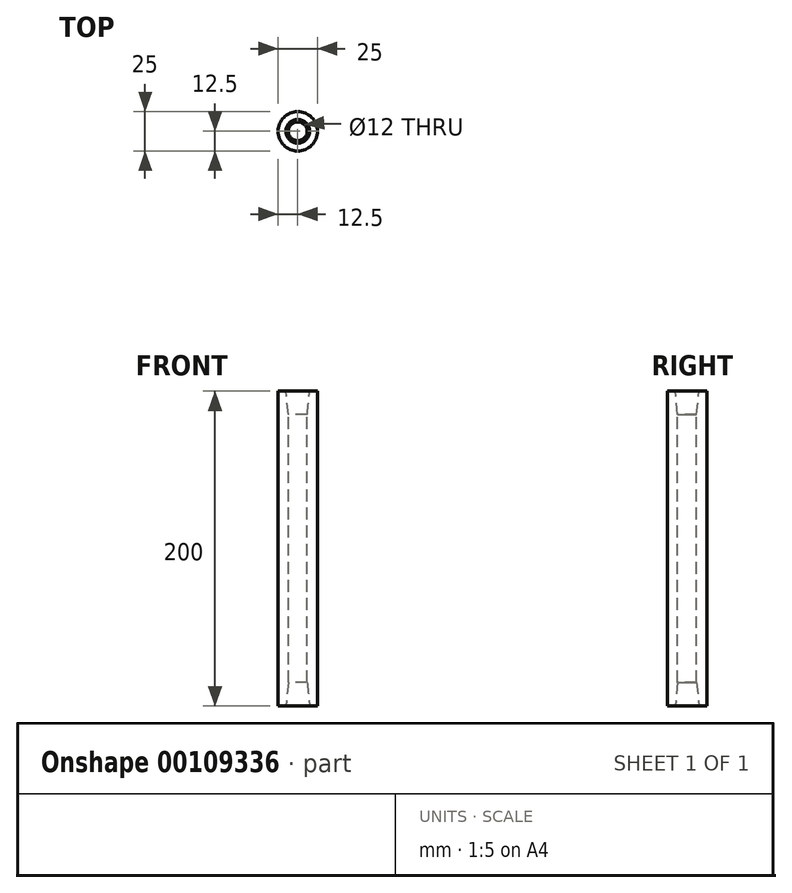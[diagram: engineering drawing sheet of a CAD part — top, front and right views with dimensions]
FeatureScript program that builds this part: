
annotation { "Feature Type Name" : "Feature", "Feature Type Description" : "" }
export const myFeature = defineFeature(function(context is Context, id is Id, definition is map)
    precondition{}
    {
        {
            var Q0;
            Q0=qCreatedBy(makeId("Front.planeOp"),FACE);
            var sketch = newSketch(context, id + "F0", { "sketchPlane" : qUnion([Q0])});
            skLineSegment(sketch, "E0.bottom", {"start": v(-6, 50) * mm, "end": v(0, 50) * mm});
            skLineSegment(sketch, "E0.top", {"start": v(-6, -120) * mm, "end": v(0, -120) * mm});
            skLineSegment(sketch, "E0.left", {"start": v(-6, 50) * mm, "end": v(-6, -120) * mm});
            skLineSegment(sketch, "E1", {"start": v(-6, 50) * mm, "end": v(-7.5, 65) * mm});
            skLineSegment(sketch, "E2", {"start": v(-7.5, 65) * mm, "end": v(0, 65) * mm});
            skLineSegment(sketch, "E3", {"start": v(-6, -120) * mm, "end": v(-7.5, -135) * mm});
            skLineSegment(sketch, "E4", {"start": v(-7.5, -135) * mm, "end": v(0, -135) * mm});
            skPoint(sketch, "E5", {"position": v(0, 50) * mm});
            skPoint(sketch, "E6", {"position": v(0, 65) * mm});
            skPoint(sketch, "E7", {"position": v(0, -120) * mm});
            skPoint(sketch, "E8", {"position": v(0, -135) * mm});
            skLineSegment(sketch, "E9", {"start": v(0, 65) * mm, "end": v(0, -135) * mm});
            skLineSegment(sketch, "E10", {"start": v(-7.5, 65) * mm, "end": v(-12.5, 65) * mm});
            skLineSegment(sketch, "E11", {"start": v(-12.5, 65) * mm, "end": v(-12.5, -135) * mm});
            skLineSegment(sketch, "E12", {"start": v(-12.5, -135) * mm, "end": v(-7.5, -135) * mm});
            skSolve(sketch);
        }
        {
            var Q0;
            Q0=makeQuery(id+"F0.imprint","IMPRINT",FACE,{"disambiguationData":[TD([[makeQuery(id+"F0.imprint","IMPRINT",EDGE,{"derivedFrom":sQuery(id+"F0.wireOp",EDGE,"E0.left")}),-1.0]])]});
            var Q1;
            Q1=sQuery(id+"F0.wireOp",EDGE,"E9");
            revolve(context, id + "F1", {"entities" : qUnion([Q0]), "axis" : qUnion([Q1]), "revolveType" : RevolveType.FULL});
        }
    });
